# Revit family: 879-109X9X-002-DN50-600
name_source: partatom
category: Pipe Accessories
units: mm (PartAtom-declared; Revit-internal decimal feet)

## family parameters
Always vertical = Yes
Cut with Voids When Loaded = No
Part Type = Valve - Breaks Into
Round Connector Dimension = Use Diameter
Shared = No
Work Plane-Based = No

## types (42) — shared parameters
879-0050-10-144009A9C99 = DN50_PN10/16
879-0050-10-144009D9C99 = DN50_PN10/16
879-0065-10-144009A9C99 = DN65_PN10/16
879-0065-10-144009D9C99 = DN65_PN10/16
879-0080-10-144009A9C99 = DN80_PN10/16
879-0080-10-144009D9C99 = DN80_PN10/16
879-0100-10-144009A9C99 = DN100_PN10/16
879-0100-10-144009D9C99 = DN100_PN10/16
879-0150-10-144009A9C99 = DN150_PN10/16
879-0150-10-144009D9C99 = DN150_PN10/16
879-0200-10-044009A9C99 = DN200_PN10
879-0200-10-044009D9C99 = DN200_PN10
879-0200-10-144009A9C99 = DN200_PN16
879-0200-10-144009D9C99 = DN200_PN16
879-0250-10-044009A9C99 = DN250_PN10
879-0250-10-044009D9C99 = DN250_PN10
879-0250-10-144009A9C99 = DN250_PN16
879-0250-10-144009D9C99 = DN250_PN16
879-0300-10-044009A9C99 = DN300_PN10
879-0300-10-044009D9C99 = DN300_PN10
879-0300-10-144009A9C99 = DN300_PN16
879-0300-10-144009D9C99 = DN300_PN16
879-0350-10-044009A9C99 = DN350_PN10
879-0350-10-044009D9C99 = DN350_PN10
879-0350-10-144009A9C99 = DN350_PN16
879-0350-10-144009D9C99 = DN350_PN16
879-0400-10-044009A9C99 = DN400_PN10
879-0400-10-044009D9C99 = DN400_PN10
879-0400-10-144009A9C99 = DN400_PN16
879-0400-10-144009D9C99 = DN400_PN16
879-0450-10-044009A9C99 = DN450_PN10
879-0450-10-044009D9C99 = DN450_PN10
879-0450-10-144009A9C99 = DN450_PN16
879-0450-10-144009D9C99 = DN450_PN16
879-0500-10-044009A9C99 = DN500_PN10
879-0500-10-044009D9C99 = DN500_PN10
879-0500-10-144009A9C99 = DN500_PN16
879-0500-10-144009D9C99 = DN500_PN16
879-0600-10-044009A9C99 = DN600_PN10
879-0600-10-044009D9C99 = DN600_PN10
879-0600-10-144009A9C99 = DN600_PN16
879-0600-10-144009D9C99 = DN600_PN16
Body_wall_thickness = 10 mm  [stored 0.0328084 ft]
Description_ = AVK SINGLE SOLENOID CONTROL VALVE
Search_Table = 879-109X9X-002-DN50-600
URL product pages = https://www.avkvalves.com

## per-type parameters (varying)
- 879-0050-10-144009A9C99_DN50_PN10/16: Body_Collar_Dia=24 mm  [stored 0.0787402 ft]; Body_Collar_Dia_2=15 mm  [stored 0.0492126 ft]; Body_Flange_Dia=64 mm; Body_Flange_Dia_2=70 mm; Body_Height_1=58 mm; Body_Height_2=29 mm; Body_Height_3=45 mm; Body_Height_4=44 mm; Body_Top_Dia=9 mm  [stored 0.0295276 ft]; Body_Top_Dia_2=8 mm  [stored 0.0262467 ft]; Body_With_Dia=58 mm; Body_With_Dia_2=58 mm; Bolt_support=153 mm; Bolt_support_2=77 mm; Bolt_support_Dia=15 mm  [stored 0.0492126 ft]; Bolt_support_lenght=45 mm; Bolt_support_lenght_2=55 mm; Bottom_profile=13 mm; D1=50 mm; D3=83 mm; DN=50 mm; Fillet_Length=6 mm  [stored 0.019685 ft]; Flange_thickness=19 mm  [stored 0.062336 ft]; H3=341 mm; H3_ref=338 mm; ID=25 mm  [stored 0.082021 ft]; ID_2=19 mm  [stored 0.062336 ft]; L=230 mm; L_ref=96 mm; PG_Dia=25 mm  [stored 0.082021 ft]; PG_Ref=38 mm; PG_depth=8 mm  [stored 0.0262467 ft]; PG_ref=35 mm  [stored 0.114829 ft]; Pilot_Dia_1=15 mm  [stored 0.0492126 ft]; Pilot_Dia_2=30 mm  [stored 0.0984252 ft]; Pilot_Dia_3=10 mm  [stored 0.0328084 ft]; Pilot_Dia_4=5 mm  [stored 0.0164042 ft]; Pilot_Dia_5=3 mm  [stored 0.00984252 ft]; Pilot_top_1=211 mm; Pilot_top_ref=45 mm; Profile1_Height=135 mm; Profile1_Length=7 mm  [stored 0.0229659 ft]; Profile1_Length_2=5 mm  [stored 0.0164042 ft]; Profile_Dia=6 mm  [stored 0.019685 ft]; Profile_Dia_2=6 mm  [stored 0.019685 ft]; Profile_Dia_3=12 mm  [stored 0.0393701 ft]; Top_Profile=92 mm; Top_Profile_Ref=97 mm; Top_Profile_Ref_2=60 mm; Top_Profile_Ref_3=225 mm; W=259 mm; W_Ref=255 mm
- 879-0050-10-144009D9C99_DN50_PN10/16: Body_Collar_Dia=24 mm  [stored 0.0787402 ft]; Body_Collar_Dia_2=15 mm  [stored 0.0492126 ft]; Body_Flange_Dia=64 mm; Body_Flange_Dia_2=70 mm; Body_Height_1=58 mm; Body_Height_2=29 mm; Body_Height_3=50 mm; Body_Height_4=44 mm; Body_Top_Dia=9 mm  [stored 0.0295276 ft]; Body_Top_Dia_2=8 mm  [stored 0.0262467 ft]; Body_With_Dia=58 mm; Body_With_Dia_2=58 mm; Bolt_support=153 mm; Bolt_support_2=77 mm; Bolt_support_Dia=15 mm  [stored 0.0492126 ft]; Bolt_support_lenght=45 mm; Bolt_support_lenght_2=55 mm; Bottom_profile=13 mm; D1=50 mm; D3=83 mm; DN=50 mm; Fillet_Length=6 mm  [stored 0.019685 ft]; Flange_thickness=19 mm  [stored 0.062336 ft]; H3=341 mm; H3_ref=338 mm; ID=25 mm  [stored 0.082021 ft]; ID_2=19 mm  [stored 0.062336 ft]; L=230 mm; L_ref=96 mm; PG_Dia=25 mm  [stored 0.082021 ft]; PG_Ref=38 mm; PG_depth=8 mm  [stored 0.0262467 ft]; PG_ref=35 mm  [stored 0.114829 ft]; Pilot_Dia_1=15 mm  [stored 0.0492126 ft]; Pilot_Dia_2=30 mm  [stored 0.0984252 ft]; Pilot_Dia_3=10 mm  [stored 0.0328084 ft]; Pilot_Dia_4=5 mm  [stored 0.0164042 ft]; Pilot_Dia_5=3 mm  [stored 0.00984252 ft]; Pilot_top_1=213 mm; Pilot_top_ref=42 mm  [stored 0.137795 ft]; Profile1_Height=145 mm; Profile1_Length=7 mm  [stored 0.0229659 ft]; Profile1_Length_2=5 mm  [stored 0.0164042 ft]; Profile_Dia=6 mm  [stored 0.019685 ft]; Profile_Dia_2=6 mm  [stored 0.019685 ft]; Profile_Dia_3=12 mm  [stored 0.0393701 ft]; Top_Profile=92 mm; Top_Profile_Ref=97 mm; Top_Profile_Ref_2=55 mm; Top_Profile_Ref_3=228 mm; W=259 mm; W_Ref=255 mm
- 879-0065-10-144009A9C99_DN65_PN10/16: Body_Collar_Dia=30 mm  [stored 0.0984252 ft]; Body_Collar_Dia_2=19 mm  [stored 0.062336 ft]; Body_Flange_Dia=81 mm; Body_Flange_Dia_2=88 mm; Body_Height_1=73 mm; Body_Height_2=36 mm; Body_Height_3=58 mm; Body_Height_4=51 mm; Body_Top_Dia=12 mm  [stored 0.0393701 ft]; Body_Top_Dia_2=10 mm  [stored 0.0328084 ft]; Body_With_Dia=73 mm; Body_With_Dia_2=73 mm; Bolt_support=193 mm; Bolt_support_2=97 mm; Bolt_support_Dia=15 mm  [stored 0.0492126 ft]; Bolt_support_lenght=53 mm; Bolt_support_lenght_2=63 mm; Bottom_profile=16 mm  [stored 0.0524934 ft]; D1=59 mm; D3=93 mm; DN=65 mm; Fillet_Length=6 mm  [stored 0.019685 ft]; Flange_thickness=19 mm  [stored 0.062336 ft]; H3=372 mm; H3_ref=369 mm; ID=33 mm; ID_2=25 mm  [stored 0.082021 ft]; L=290 mm; L_ref=121 mm; PG_Dia=33 mm; PG_Ref=48 mm; PG_depth=8 mm  [stored 0.0262467 ft]; PG_ref=43 mm; Pilot_Dia_1=18 mm; Pilot_Dia_2=35 mm  [stored 0.114829 ft]; Pilot_Dia_3=12 mm  [stored 0.0393701 ft]; Pilot_Dia_4=6 mm  [stored 0.019685 ft]; Pilot_Dia_5=4 mm  [stored 0.0131234 ft]; Pilot_top_1=239 mm; Pilot_top_ref=37 mm; Profile1_Height=152 mm; Profile1_Length=8 mm  [stored 0.0262467 ft]; Profile1_Length_2=5 mm  [stored 0.0164042 ft]; Profile_Dia=6 mm  [stored 0.019685 ft]; Profile_Dia_2=6 mm  [stored 0.019685 ft]; Profile_Dia_3=12 mm  [stored 0.0393701 ft]; Top_Profile=116 mm; Top_Profile_Ref=121 mm; Top_Profile_Ref_2=62 mm; Top_Profile_Ref_3=245 mm; W=275 mm; W_Ref=271 mm
- 879-0065-10-144009D9C99_DN65_PN10/16: Body_Collar_Dia=30 mm  [stored 0.0984252 ft]; Body_Collar_Dia_2=19 mm  [stored 0.062336 ft]; Body_Flange_Dia=81 mm; Body_Flange_Dia_2=88 mm; Body_Height_1=73 mm; Body_Height_2=36 mm; Body_Height_3=73 mm; Body_Height_4=51 mm; Body_Top_Dia=12 mm  [stored 0.0393701 ft]; Body_Top_Dia_2=10 mm  [stored 0.0328084 ft]; Body_With_Dia=73 mm; Body_With_Dia_2=73 mm; Bolt_support=193 mm; Bolt_support_2=97 mm; Bolt_support_Dia=15 mm  [stored 0.0492126 ft]; Bolt_support_lenght=53 mm; Bolt_support_lenght_2=63 mm; Bottom_profile=16 mm  [stored 0.0524934 ft]; D1=59 mm; D3=93 mm; DN=65 mm; Fillet_Length=6 mm  [stored 0.019685 ft]; Flange_thickness=19 mm  [stored 0.062336 ft]; H3=372 mm; H3_ref=369 mm; ID=33 mm; ID_2=25 mm  [stored 0.082021 ft]; L=290 mm; L_ref=121 mm; PG_Dia=33 mm; PG_Ref=48 mm; PG_depth=8 mm  [stored 0.0262467 ft]; PG_ref=43 mm; Pilot_Dia_1=18 mm; Pilot_Dia_2=35 mm  [stored 0.114829 ft]; Pilot_Dia_3=12 mm  [stored 0.0393701 ft]; Pilot_Dia_4=6 mm  [stored 0.019685 ft]; Pilot_Dia_5=4 mm  [stored 0.0131234 ft]; Pilot_top_1=246 mm; Pilot_top_ref=30 mm  [stored 0.0984252 ft]; Profile1_Height=170 mm; Profile1_Length=8 mm  [stored 0.0262467 ft]; Profile1_Length_2=5 mm  [stored 0.0164042 ft]; Profile_Dia=6 mm  [stored 0.019685 ft]; Profile_Dia_2=6 mm  [stored 0.019685 ft]; Profile_Dia_3=12 mm  [stored 0.0393701 ft]; Top_Profile=116 mm; Top_Profile_Ref=121 mm; Top_Profile_Ref_2=53 mm; Top_Profile_Ref_3=250 mm; W=275 mm; W_Ref=271 mm
- 879-0080-10-144009A9C99_DN80_PN10/16: Body_Collar_Dia=32 mm  [stored 0.104987 ft]; Body_Collar_Dia_2=21 mm  [stored 0.0688976 ft]; Body_Flange_Dia=86 mm; Body_Flange_Dia_2=94 mm; Body_Height_1=78 mm; Body_Height_2=39 mm  [stored 0.127953 ft]; Body_Height_3=62 mm; Body_Height_4=54 mm; Body_Top_Dia=12 mm  [stored 0.0393701 ft]; Body_Top_Dia_2=10 mm  [stored 0.0328084 ft]; Body_With_Dia=78 mm; Body_With_Dia_2=78 mm; Bolt_support=207 mm; Bolt_support_2=103 mm; Bolt_support_Dia=15 mm  [stored 0.0492126 ft]; Bolt_support_lenght=60 mm; Bolt_support_lenght_2=70 mm; Bottom_profile=20 mm  [stored 0.0656168 ft]; D1=66 mm; D3=100 mm; DN=80 mm; Fillet_Length=6 mm  [stored 0.019685 ft]; Flange_thickness=19 mm  [stored 0.062336 ft]; H3=387 mm; H3_ref=384 mm; ID=40 mm  [stored 0.131234 ft]; ID_2=31 mm  [stored 0.101706 ft]; L=310 mm; L_ref=129 mm; PG_Dia=40 mm  [stored 0.131234 ft]; PG_Ref=52 mm; PG_depth=8 mm  [stored 0.0262467 ft]; PG_ref=50 mm; Pilot_Dia_1=20 mm  [stored 0.0656168 ft]; Pilot_Dia_2=39 mm  [stored 0.127953 ft]; Pilot_Dia_3=13 mm; Pilot_Dia_4=7 mm  [stored 0.0229659 ft]; Pilot_Dia_5=4 mm  [stored 0.0131234 ft]; Pilot_top_1=249 mm; Pilot_top_ref=35 mm  [stored 0.114829 ft]; Profile1_Height=179 mm; Profile1_Length=8 mm  [stored 0.0262467 ft]; Profile1_Length_2=6 mm  [stored 0.019685 ft]; Profile_Dia=6 mm  [stored 0.019685 ft]; Profile_Dia_2=6 mm  [stored 0.019685 ft]; Profile_Dia_3=12 mm  [stored 0.0393701 ft]; Top_Profile=124 mm; Top_Profile_Ref=129 mm; Top_Profile_Ref_2=53 mm; Top_Profile_Ref_3=258 mm; W=290 mm; W_Ref=286 mm
- 879-0080-10-144009D9C99_DN80_PN10/16: Body_Collar_Dia=32 mm  [stored 0.104987 ft]; Body_Collar_Dia_2=21 mm  [stored 0.0688976 ft]; Body_Flange_Dia=86 mm; Body_Flange_Dia_2=94 mm; Body_Height_1=78 mm; Body_Height_2=39 mm  [stored 0.127953 ft]; Body_Height_3=78 mm; Body_Height_4=54 mm; Body_Top_Dia=12 mm  [stored 0.0393701 ft]; Body_Top_Dia_2=10 mm  [stored 0.0328084 ft]; Body_With_Dia=78 mm; Body_With_Dia_2=78 mm; Bolt_support=207 mm; Bolt_support_2=103 mm; Bolt_support_Dia=15 mm  [stored 0.0492126 ft]; Bolt_support_lenght=60 mm; Bolt_support_lenght_2=70 mm; Bottom_profile=20 mm  [stored 0.0656168 ft]; D1=66 mm; D3=100 mm; DN=80 mm; Fillet_Length=6 mm  [stored 0.019685 ft]; Flange_thickness=19 mm  [stored 0.062336 ft]; H3=387 mm; H3_ref=384 mm; ID=40 mm  [stored 0.131234 ft]; ID_2=31 mm  [stored 0.101706 ft]; L=310 mm; L_ref=129 mm; PG_Dia=40 mm  [stored 0.131234 ft]; PG_Ref=52 mm; PG_depth=8 mm  [stored 0.0262467 ft]; PG_ref=50 mm; Pilot_Dia_1=20 mm  [stored 0.0656168 ft]; Pilot_Dia_2=39 mm  [stored 0.127953 ft]; Pilot_Dia_3=13 mm; Pilot_Dia_4=7 mm  [stored 0.0229659 ft]; Pilot_Dia_5=4 mm  [stored 0.0131234 ft]; Pilot_top_1=256 mm; Pilot_top_ref=28 mm  [stored 0.0918635 ft]; Profile1_Height=168 mm; Profile1_Length=8 mm  [stored 0.0262467 ft]; Profile1_Length_2=6 mm  [stored 0.019685 ft]; Profile_Dia=6 mm  [stored 0.019685 ft]; Profile_Dia_2=6 mm  [stored 0.019685 ft]; Profile_Dia_3=12 mm  [stored 0.0393701 ft]; Top_Profile=124 mm; Top_Profile_Ref=129 mm; Top_Profile_Ref_2=58 mm; Top_Profile_Ref_3=255 mm; W=290 mm; W_Ref=286 mm
- 879-0100-10-144009A9C99_DN100_PN10/16: Body_Collar_Dia=36 mm; Body_Collar_Dia_2=23 mm  [stored 0.0754593 ft]; Body_Flange_Dia=97 mm; Body_Flange_Dia_2=106 mm; Body_Height_1=88 mm; Body_Height_2=44 mm; Body_Height_3=59 mm; Body_Height_4=59 mm; Body_Top_Dia=14 mm  [stored 0.0459318 ft]; Body_Top_Dia_2=12 mm  [stored 0.0393701 ft]; Body_With_Dia=88 mm; Body_With_Dia_2=88 mm; Bolt_support=233 mm; Bolt_support_2=117 mm; Bolt_support_Dia=15 mm  [stored 0.0492126 ft]; Bolt_support_lenght=70 mm; Bolt_support_lenght_2=80 mm; Bottom_profile=25 mm  [stored 0.082021 ft]; D1=78 mm; D3=110 mm; DN=100 mm; Fillet_Length=6 mm  [stored 0.019685 ft]; Flange_thickness=19 mm  [stored 0.062336 ft]; H3=410 mm; H3_ref=407 mm; ID=50 mm; ID_2=38 mm; L=350 mm; L_ref=146 mm; PG_Dia=50 mm; PG_Ref=58 mm; PG_depth=8 mm  [stored 0.0262467 ft]; PG_ref=60 mm; Pilot_Dia_1=22 mm  [stored 0.0721785 ft]; Pilot_Dia_2=44 mm; Pilot_Dia_3=15 mm  [stored 0.0492126 ft]; Pilot_Dia_4=7 mm  [stored 0.0229659 ft]; Pilot_Dia_5=5 mm  [stored 0.0164042 ft]; Pilot_top_1=261 mm; Pilot_top_ref=36 mm; Profile1_Height=185 mm; Profile1_Length=9 mm  [stored 0.0295276 ft]; Profile1_Length_2=6 mm  [stored 0.019685 ft]; Profile_Dia=6 mm  [stored 0.019685 ft]; Profile_Dia_2=6 mm  [stored 0.019685 ft]; Profile_Dia_3=12 mm  [stored 0.0393701 ft]; Top_Profile=140 mm; Top_Profile_Ref=145 mm; Top_Profile_Ref_2=56 mm; Top_Profile_Ref_3=269 mm; W=310 mm; W_Ref=306 mm
- 879-0100-10-144009D9C99_DN100_PN10/16: Body_Collar_Dia=36 mm; Body_Collar_Dia_2=23 mm  [stored 0.0754593 ft]; Body_Flange_Dia=97 mm; Body_Flange_Dia_2=106 mm; Body_Height_1=88 mm; Body_Height_2=44 mm; Body_Height_3=70 mm; Body_Height_4=59 mm; Body_Top_Dia=14 mm  [stored 0.0459318 ft]; Body_Top_Dia_2=12 mm  [stored 0.0393701 ft]; Body_With_Dia=88 mm; Body_With_Dia_2=88 mm; Bolt_support=233 mm; Bolt_support_2=117 mm; Bolt_support_Dia=15 mm  [stored 0.0492126 ft]; Bolt_support_lenght=70 mm; Bolt_support_lenght_2=80 mm; Bottom_profile=25 mm  [stored 0.082021 ft]; D1=78 mm; D3=110 mm; DN=100 mm; Fillet_Length=6 mm  [stored 0.019685 ft]; Flange_thickness=19 mm  [stored 0.062336 ft]; H3=410 mm; H3_ref=407 mm; ID=50 mm; ID_2=39 mm  [stored 0.127953 ft]; L=350 mm; L_ref=146 mm; PG_Dia=50 mm; PG_Ref=58 mm; PG_depth=8 mm  [stored 0.0262467 ft]; PG_ref=60 mm; Pilot_Dia_1=22 mm  [stored 0.0721785 ft]; Pilot_Dia_2=44 mm; Pilot_Dia_3=15 mm  [stored 0.0492126 ft]; Pilot_Dia_4=7 mm  [stored 0.0229659 ft]; Pilot_Dia_5=5 mm  [stored 0.0164042 ft]; Pilot_top_1=267 mm; Pilot_top_ref=30 mm  [stored 0.0984252 ft]; Profile1_Height=176 mm; Profile1_Length=9 mm  [stored 0.0295276 ft]; Profile1_Length_2=6 mm  [stored 0.019685 ft]; Profile_Dia=6 mm  [stored 0.019685 ft]; Profile_Dia_2=6 mm  [stored 0.019685 ft]; Profile_Dia_3=12 mm  [stored 0.0393701 ft]; Top_Profile=140 mm; Top_Profile_Ref=145 mm; Top_Profile_Ref_2=61 mm; Top_Profile_Ref_3=267 mm; W=310 mm; W_Ref=306 mm
- 879-0150-10-144009A9C99_DN150_PN10/16: Body_Collar_Dia=50 mm; Body_Collar_Dia_2=32 mm  [stored 0.104987 ft]; Body_Flange_Dia=133 mm; Body_Flange_Dia_2=145 mm; Body_Height_1=120 mm; Body_Height_2=60 mm; Body_Height_3=60 mm; Body_Height_4=75 mm; Body_Top_Dia=19 mm  [stored 0.062336 ft]; Body_Top_Dia_2=16 mm  [stored 0.0524934 ft]; Body_With_Dia=120 mm; Body_With_Dia_2=120 mm; Bolt_support=320 mm; Bolt_support_2=160 mm; Bolt_support_Dia=20 mm  [stored 0.0656168 ft]; Bolt_support_lenght=95 mm; Bolt_support_lenght_2=105 mm; Bottom_profile=38 mm; D1=106 mm; D3=143 mm; DN=150 mm; Fillet_Length=8 mm  [stored 0.0262467 ft]; Flange_thickness=19 mm  [stored 0.062336 ft]; H3=543 mm; H3_ref=539 mm; ID=75 mm; ID_2=58 mm; L=480 mm; L_ref=200 mm; PG_Dia=50 mm; PG_Ref=80 mm; PG_depth=11 mm; PG_ref=85 mm; Pilot_Dia_1=31 mm  [stored 0.101706 ft]; Pilot_Dia_2=62 mm; Pilot_Dia_3=21 mm  [stored 0.0688976 ft]; Pilot_Dia_4=10 mm  [stored 0.0328084 ft]; Pilot_Dia_5=7 mm  [stored 0.0229659 ft]; Pilot_top_1=336 mm; Pilot_top_ref=61 mm; Profile1_Height=230 mm; Profile1_Length=12 mm  [stored 0.0393701 ft]; Profile1_Length_2=8 mm  [stored 0.0262467 ft]; Profile_Dia=8 mm  [stored 0.0262467 ft]; Profile_Dia_2=8 mm  [stored 0.0262467 ft]; Profile_Dia_3=16 mm  [stored 0.0524934 ft]; Top_Profile=192 mm; Top_Profile_Ref=197 mm; Top_Profile_Ref_2=83 mm; Top_Profile_Ref_3=355 mm; W=375 mm; W_Ref=369 mm
- 879-0150-10-144009D9C99_DN150_PN10/16: Body_Collar_Dia=50 mm; Body_Collar_Dia_2=32 mm  [stored 0.104987 ft]; Body_Flange_Dia=133 mm; Body_Flange_Dia_2=145 mm; Body_Height_1=120 mm; Body_Height_2=60 mm; Body_Height_3=68 mm; Body_Height_4=75 mm; Body_Top_Dia=19 mm  [stored 0.062336 ft]; Body_Top_Dia_2=16 mm  [stored 0.0524934 ft]; Body_With_Dia=120 mm; Body_With_Dia_2=120 mm; Bolt_support=320 mm; Bolt_support_2=160 mm; Bolt_support_Dia=20 mm  [stored 0.0656168 ft]; Bolt_support_lenght=95 mm; Bolt_support_lenght_2=105 mm; Bottom_profile=38 mm; D1=106 mm; D3=143 mm; DN=150 mm; Fillet_Length=8 mm  [stored 0.0262467 ft]; Flange_thickness=19 mm  [stored 0.062336 ft]; H3=543 mm; H3_ref=539 mm; ID=75 mm; ID_2=58 mm; L=480 mm; L_ref=200 mm; PG_Dia=50 mm; PG_Ref=80 mm; PG_depth=11 mm; PG_ref=85 mm; Pilot_Dia_1=31 mm  [stored 0.101706 ft]; Pilot_Dia_2=62 mm; Pilot_Dia_3=21 mm  [stored 0.0688976 ft]; Pilot_Dia_4=10 mm  [stored 0.0328084 ft]; Pilot_Dia_5=7 mm  [stored 0.0229659 ft]; Pilot_top_1=340 mm; Pilot_top_ref=57 mm; Profile1_Height=230 mm; Profile1_Length=12 mm  [stored 0.0393701 ft]; Profile1_Length_2=8 mm  [stored 0.0262467 ft]; Profile_Dia=8 mm  [stored 0.0262467 ft]; Profile_Dia_2=8 mm  [stored 0.0262467 ft]; Profile_Dia_3=16 mm  [stored 0.0524934 ft]; Top_Profile=192 mm; Top_Profile_Ref=197 mm; Top_Profile_Ref_2=83 mm; Top_Profile_Ref_3=355 mm; W=375 mm; W_Ref=369 mm
- 879-0200-10-044009A9C99_DN200_PN10: Body_Collar_Dia=63 mm; Body_Collar_Dia_2=40 mm  [stored 0.131234 ft]; Body_Flange_Dia=167 mm; Body_Flange_Dia_2=182 mm; Body_Height_1=150 mm; Body_Height_2=75 mm; Body_Height_3=75 mm; Body_Height_4=90 mm; Body_Top_Dia=24 mm  [stored 0.0787402 ft]; Body_Top_Dia_2=20 mm  [stored 0.0656168 ft]; Body_With_Dia=150 mm; Body_With_Dia_2=150 mm; Bolt_support=400 mm; Bolt_support_2=200 mm; Bolt_support_Dia=25 mm  [stored 0.082021 ft]; Bolt_support_lenght=120 mm; Bolt_support_lenght_2=130 mm; Bottom_profile=50 mm; D1=133 mm; D3=170 mm; DN=200 mm; Fillet_Length=10 mm  [stored 0.0328084 ft]; Flange_thickness=20 mm  [stored 0.0656168 ft]; H3=657 mm; H3_ref=652 mm; ID=100 mm; ID_2=77 mm; L=600 mm; L_ref=250 mm; PG_Dia=67 mm; PG_Ref=100 mm; PG_depth=14 mm  [stored 0.0459318 ft]; PG_ref=110 mm; Pilot_Dia_1=39 mm  [stored 0.127953 ft]; Pilot_Dia_2=77 mm; Pilot_Dia_3=26 mm; Pilot_Dia_4=13 mm; Pilot_Dia_5=9 mm  [stored 0.0295276 ft]; Pilot_top_1=409 mm; Pilot_top_ref=74 mm; Profile1_Height=273 mm; Profile1_Length=14 mm  [stored 0.0459318 ft]; Profile1_Length_2=9 mm  [stored 0.0295276 ft]; Profile_Dia=10 mm  [stored 0.0328084 ft]; Profile_Dia_2=10 mm  [stored 0.0328084 ft]; Profile_Dia_3=20 mm  [stored 0.0656168 ft]; Top_Profile=240 mm; Top_Profile_Ref=245 mm; Top_Profile_Ref_2=105 mm; Top_Profile_Ref_3=430 mm; W=445 mm; W_Ref=438 mm
- 879-0200-10-044009D9C99_DN200_PN10: Body_Collar_Dia=63 mm; Body_Collar_Dia_2=40 mm  [stored 0.131234 ft]; Body_Flange_Dia=167 mm; Body_Flange_Dia_2=182 mm; Body_Height_1=150 mm; Body_Height_2=75 mm; Body_Height_3=100 mm; Body_Height_4=90 mm; Body_Top_Dia=24 mm  [stored 0.0787402 ft]; Body_Top_Dia_2=20 mm  [stored 0.0656168 ft]; Body_With_Dia=150 mm; Body_With_Dia_2=150 mm; Bolt_support=400 mm; Bolt_support_2=200 mm; Bolt_support_Dia=25 mm  [stored 0.082021 ft]; Bolt_support_lenght=120 mm; Bolt_support_lenght_2=130 mm; Bottom_profile=50 mm; D1=133 mm; D3=170 mm; DN=200 mm; Fillet_Length=10 mm  [stored 0.0328084 ft]; Flange_thickness=20 mm  [stored 0.0656168 ft]; H3=657 mm; H3_ref=652 mm; ID=100 mm; ID_2=77 mm; L=600 mm; L_ref=250 mm; PG_Dia=67 mm; PG_Ref=100 mm; PG_depth=14 mm  [stored 0.0459318 ft]; PG_ref=110 mm; Pilot_Dia_1=39 mm  [stored 0.127953 ft]; Pilot_Dia_2=77 mm; Pilot_Dia_3=26 mm; Pilot_Dia_4=13 mm; Pilot_Dia_5=9 mm  [stored 0.0295276 ft]; Pilot_top_1=421 mm; Pilot_top_ref=61 mm; Profile1_Height=275 mm; Profile1_Length=14 mm  [stored 0.0459318 ft]; Profile1_Length_2=9 mm  [stored 0.0295276 ft]; Profile_Dia=10 mm  [stored 0.0328084 ft]; Profile_Dia_2=10 mm  [stored 0.0328084 ft]; Profile_Dia_3=20 mm  [stored 0.0656168 ft]; Top_Profile=240 mm; Top_Profile_Ref=245 mm; Top_Profile_Ref_2=104 mm; Top_Profile_Ref_3=430 mm; W=445 mm; W_Ref=438 mm
- 879-0200-10-144009A9C99_DN200_PN16: Body_Collar_Dia=63 mm; Body_Collar_Dia_2=40 mm  [stored 0.131234 ft]; Body_Flange_Dia=167 mm; Body_Flange_Dia_2=182 mm; Body_Height_1=150 mm; Body_Height_2=75 mm; Body_Height_3=75 mm; Body_Height_4=90 mm; Body_Top_Dia=24 mm  [stored 0.0787402 ft]; Body_Top_Dia_2=20 mm  [stored 0.0656168 ft]; Body_With_Dia=150 mm; Body_With_Dia_2=150 mm; Bolt_support=400 mm; Bolt_support_2=200 mm; Bolt_support_Dia=25 mm  [stored 0.082021 ft]; Bolt_support_lenght=120 mm; Bolt_support_lenght_2=130 mm; Bottom_profile=50 mm; D1=133 mm; D3=170 mm; DN=200 mm; Fillet_Length=10 mm  [stored 0.0328084 ft]; Flange_thickness=20 mm  [stored 0.0656168 ft]; H3=657 mm; H3_ref=652 mm; ID=100 mm; ID_2=77 mm; L=600 mm; L_ref=250 mm; PG_Dia=67 mm; PG_Ref=100 mm; PG_depth=14 mm  [stored 0.0459318 ft]; PG_ref=110 mm; Pilot_Dia_1=39 mm  [stored 0.127953 ft]; Pilot_Dia_2=77 mm; Pilot_Dia_3=26 mm; Pilot_Dia_4=13 mm; Pilot_Dia_5=9 mm  [stored 0.0295276 ft]; Pilot_top_1=409 mm; Pilot_top_ref=74 mm; Profile1_Height=273 mm; Profile1_Length=14 mm  [stored 0.0459318 ft]; Profile1_Length_2=9 mm  [stored 0.0295276 ft]; Profile_Dia=10 mm  [stored 0.0328084 ft]; Profile_Dia_2=10 mm  [stored 0.0328084 ft]; Profile_Dia_3=20 mm  [stored 0.0656168 ft]; Top_Profile=240 mm; Top_Profile_Ref=245 mm; Top_Profile_Ref_2=105 mm; Top_Profile_Ref_3=430 mm; W=445 mm; W_Ref=438 mm
- 879-0200-10-144009D9C99_DN200_PN16: Body_Collar_Dia=63 mm; Body_Collar_Dia_2=40 mm  [stored 0.131234 ft]; Body_Flange_Dia=167 mm; Body_Flange_Dia_2=182 mm; Body_Height_1=150 mm; Body_Height_2=75 mm; Body_Height_3=86 mm; Body_Height_4=90 mm; Body_Top_Dia=24 mm  [stored 0.0787402 ft]; Body_Top_Dia_2=20 mm  [stored 0.0656168 ft]; Body_With_Dia=150 mm; Body_With_Dia_2=150 mm; Bolt_support=400 mm; Bolt_support_2=200 mm; Bolt_support_Dia=25 mm  [stored 0.082021 ft]; Bolt_support_lenght=120 mm; Bolt_support_lenght_2=130 mm; Bottom_profile=50 mm; D1=133 mm; D3=170 mm; DN=200 mm; Fillet_Length=10 mm  [stored 0.0328084 ft]; Flange_thickness=20 mm  [stored 0.0656168 ft]; H3=657 mm; H3_ref=652 mm; ID=100 mm; ID_2=77 mm; L=600 mm; L_ref=250 mm; PG_Dia=67 mm; PG_Ref=100 mm; PG_depth=14 mm  [stored 0.0459318 ft]; PG_ref=110 mm; Pilot_Dia_1=39 mm  [stored 0.127953 ft]; Pilot_Dia_2=77 mm; Pilot_Dia_3=26 mm; Pilot_Dia_4=13 mm; Pilot_Dia_5=9 mm  [stored 0.0295276 ft]; Pilot_top_1=414 mm; Pilot_top_ref=68 mm; Profile1_Height=275 mm; Profile1_Length=14 mm  [stored 0.0459318 ft]; Profile1_Length_2=9 mm  [stored 0.0295276 ft]; Profile_Dia=10 mm  [stored 0.0328084 ft]; Profile_Dia_2=10 mm  [stored 0.0328084 ft]; Profile_Dia_3=20 mm  [stored 0.0656168 ft]; Top_Profile=240 mm; Top_Profile_Ref=245 mm; Top_Profile_Ref_2=104 mm; Top_Profile_Ref_3=430 mm; W=445 mm; W_Ref=438 mm
- 879-0250-10-044009A9C99_DN250_PN10: Body_Collar_Dia=76 mm; Body_Collar_Dia_2=49 mm; Body_Flange_Dia=203 mm; Body_Flange_Dia_2=221 mm; Body_Height_1=183 mm; Body_Height_2=91 mm; Body_Height_3=81 mm; Body_Height_4=106 mm; Body_Top_Dia=29 mm; Body_Top_Dia_2=24 mm  [stored 0.0787402 ft]; Body_With_Dia=183 mm; Body_With_Dia_2=183 mm; Bolt_support=487 mm; Bolt_support_2=243 mm; Bolt_support_Dia=25 mm  [stored 0.082021 ft]; Bolt_support_lenght=145 mm; Bolt_support_lenght_2=155 mm; Bottom_profile=63 mm; D1=160 mm; D3=198 mm; DN=250 mm; Fillet_Length=10 mm  [stored 0.0328084 ft]; Flange_thickness=22 mm  [stored 0.0721785 ft]; H3=692 mm; H3_ref=687 mm; ID=125 mm; ID_2=96 mm; L=730 mm; L_ref=304 mm; PG_Dia=83 mm; PG_Ref=122 mm; PG_depth=14 mm  [stored 0.0459318 ft]; PG_ref=135 mm; Pilot_Dia_1=46 mm; Pilot_Dia_2=92 mm; Pilot_Dia_3=31 mm  [stored 0.101706 ft]; Pilot_Dia_4=15 mm  [stored 0.0492126 ft]; Pilot_Dia_5=10 mm  [stored 0.0328084 ft]; Pilot_top_1=440 mm; Pilot_top_ref=50 mm; Profile1_Height=327 mm; Profile1_Length=16 mm  [stored 0.0524934 ft]; Profile1_Length_2=11 mm; Profile_Dia=10 mm  [stored 0.0328084 ft]; Profile_Dia_2=10 mm  [stored 0.0328084 ft]; Profile_Dia_3=20 mm  [stored 0.0656168 ft]; Top_Profile=292 mm; Top_Profile_Ref=297 mm; Top_Profile_Ref_2=81 mm; Top_Profile_Ref_3=449 mm; W=525 mm; W_Ref=518 mm
- 879-0250-10-044009D9C99_DN250_PN10: Body_Collar_Dia=76 mm; Body_Collar_Dia_2=49 mm; Body_Flange_Dia=203 mm; Body_Flange_Dia_2=221 mm; Body_Height_1=183 mm; Body_Height_2=91 mm; Body_Height_3=105 mm; Body_Height_4=106 mm; Body_Top_Dia=29 mm; Body_Top_Dia_2=24 mm  [stored 0.0787402 ft]; Body_With_Dia=183 mm; Body_With_Dia_2=183 mm; Bolt_support=487 mm; Bolt_support_2=243 mm; Bolt_support_Dia=25 mm  [stored 0.082021 ft]; Bolt_support_lenght=145 mm; Bolt_support_lenght_2=155 mm; Bottom_profile=63 mm; D1=160 mm; D3=198 mm; DN=250 mm; Fillet_Length=10 mm  [stored 0.0328084 ft]; Flange_thickness=22 mm  [stored 0.0721785 ft]; H3=692 mm; H3_ref=687 mm; ID=125 mm; ID_2=96 mm; L=730 mm; L_ref=304 mm; PG_Dia=83 mm; PG_Ref=122 mm; PG_depth=14 mm  [stored 0.0459318 ft]; PG_ref=135 mm; Pilot_Dia_1=46 mm; Pilot_Dia_2=92 mm; Pilot_Dia_3=31 mm  [stored 0.101706 ft]; Pilot_Dia_4=15 mm  [stored 0.0492126 ft]; Pilot_Dia_5=10 mm  [stored 0.0328084 ft]; Pilot_top_1=451 mm; Pilot_top_ref=38 mm; Profile1_Height=330 mm; Profile1_Length=16 mm  [stored 0.0524934 ft]; Profile1_Length_2=11 mm; Profile_Dia=10 mm  [stored 0.0328084 ft]; Profile_Dia_2=10 mm  [stored 0.0328084 ft]; Profile_Dia_3=20 mm  [stored 0.0656168 ft]; Top_Profile=292 mm; Top_Profile_Ref=297 mm; Top_Profile_Ref_2=80 mm; Top_Profile_Ref_3=450 mm; W=525 mm; W_Ref=518 mm
- 879-0250-10-144009A9C99_DN250_PN16: Body_Collar_Dia=76 mm; Body_Collar_Dia_2=49 mm; Body_Flange_Dia=203 mm; Body_Flange_Dia_2=221 mm; Body_Height_1=183 mm; Body_Height_2=91 mm; Body_Height_3=81 mm; Body_Height_4=106 mm; Body_Top_Dia=29 mm; Body_Top_Dia_2=24 mm  [stored 0.0787402 ft]; Body_With_Dia=183 mm; Body_With_Dia_2=183 mm; Bolt_support=487 mm; Bolt_support_2=243 mm; Bolt_support_Dia=25 mm  [stored 0.082021 ft]; Bolt_support_lenght=145 mm; Bolt_support_lenght_2=155 mm; Bottom_profile=63 mm; D1=160 mm; D3=203 mm; DN=250 mm; Fillet_Length=10 mm  [stored 0.0328084 ft]; Flange_thickness=22 mm  [stored 0.0721785 ft]; H3=692 mm; H3_ref=687 mm; ID=125 mm; ID_2=96 mm; L=730 mm; L_ref=304 mm; PG_Dia=83 mm; PG_Ref=122 mm; PG_depth=14 mm  [stored 0.0459318 ft]; PG_ref=135 mm; Pilot_Dia_1=47 mm; Pilot_Dia_2=94 mm; Pilot_Dia_3=31 mm  [stored 0.101706 ft]; Pilot_Dia_4=16 mm  [stored 0.0524934 ft]; Pilot_Dia_5=10 mm  [stored 0.0328084 ft]; Pilot_top_1=437 mm; Pilot_top_ref=47 mm; Profile1_Height=335 mm; Profile1_Length=17 mm; Profile1_Length_2=11 mm; Profile_Dia=10 mm  [stored 0.0328084 ft]; Profile_Dia_2=10 mm  [stored 0.0328084 ft]; Profile_Dia_3=20 mm  [stored 0.0656168 ft]; Top_Profile=292 mm; Top_Profile_Ref=297 mm; Top_Profile_Ref_2=75 mm; Top_Profile_Ref_3=447 mm; W=525 mm; W_Ref=518 mm
- 879-0250-10-144009D9C99_DN250_PN16: Body_Collar_Dia=76 mm; Body_Collar_Dia_2=49 mm; Body_Flange_Dia=203 mm; Body_Flange_Dia_2=221 mm; Body_Height_1=183 mm; Body_Height_2=91 mm; Body_Height_3=81 mm; Body_Height_4=106 mm; Body_Top_Dia=29 mm; Body_Top_Dia_2=24 mm  [stored 0.0787402 ft]; Body_With_Dia=183 mm; Body_With_Dia_2=183 mm; Bolt_support=487 mm; Bolt_support_2=243 mm; Bolt_support_Dia=25 mm  [stored 0.082021 ft]; Bolt_support_lenght=145 mm; Bolt_support_lenght_2=155 mm; Bottom_profile=63 mm; D1=160 mm; D3=203 mm; DN=250 mm; Fillet_Length=10 mm  [stored 0.0328084 ft]; Flange_thickness=22 mm  [stored 0.0721785 ft]; H3=692 mm; H3_ref=687 mm; ID=125 mm; ID_2=96 mm; L=730 mm; L_ref=304 mm; PG_Dia=83 mm; PG_Ref=122 mm; PG_depth=14 mm  [stored 0.0459318 ft]; PG_ref=135 mm; Pilot_Dia_1=47 mm; Pilot_Dia_2=94 mm; Pilot_Dia_3=31 mm  [stored 0.101706 ft]; Pilot_Dia_4=16 mm  [stored 0.0524934 ft]; Pilot_Dia_5=10 mm  [stored 0.0328084 ft]; Pilot_top_1=437 mm; Pilot_top_ref=47 mm; Profile1_Height=350 mm; Profile1_Length=17 mm; Profile1_Length_2=11 mm; Profile_Dia=10 mm  [stored 0.0328084 ft]; Profile_Dia_2=10 mm  [stored 0.0328084 ft]; Profile_Dia_3=20 mm  [stored 0.0656168 ft]; Top_Profile=292 mm; Top_Profile_Ref=297 mm; Top_Profile_Ref_2=67 mm; Top_Profile_Ref_3=451 mm; W=525 mm; W_Ref=518 mm
- 879-0300-10-044009A9C99_DN300_PN10: Body_Collar_Dia=89 mm; Body_Collar_Dia_2=57 mm; Body_Flange_Dia=236 mm; Body_Flange_Dia_2=258 mm; Body_Height_1=213 mm; Body_Height_2=106 mm; Body_Height_3=95 mm; Body_Height_4=121 mm; Body_Top_Dia=34 mm; Body_Top_Dia_2=28 mm  [stored 0.0918635 ft]; Body_With_Dia=213 mm; Body_With_Dia_2=213 mm; Bolt_support=567 mm; Bolt_support_2=283 mm; Bolt_support_Dia=25 mm  [stored 0.082021 ft]; Bolt_support_lenght=170 mm; Bolt_support_lenght_2=180 mm; Bottom_profile=75 mm; D1=185 mm; D3=223 mm; DN=300 mm; Fillet_Length=10 mm  [stored 0.0328084 ft]; Flange_thickness=25 mm  [stored 0.082021 ft]; H3=761 mm; H3_ref=756 mm; ID=150 mm; ID_2=115 mm; L=850 mm; L_ref=354 mm; PG_Dia=100 mm; PG_Ref=142 mm; PG_depth=14 mm  [stored 0.0459318 ft]; PG_ref=160 mm; Pilot_Dia_1=53 mm; Pilot_Dia_2=105 mm; Pilot_Dia_3=35 mm  [stored 0.114829 ft]; Pilot_Dia_4=18 mm; Pilot_Dia_5=12 mm  [stored 0.0393701 ft]; Pilot_top_1=491 mm; Pilot_top_ref=43 mm; Profile1_Height=361 mm; Profile1_Length=19 mm  [stored 0.062336 ft]; Profile1_Length_2=12 mm  [stored 0.0393701 ft]; Profile_Dia=10 mm  [stored 0.0328084 ft]; Profile_Dia_2=10 mm  [stored 0.0328084 ft]; Profile_Dia_3=20 mm  [stored 0.0656168 ft]; Top_Profile=340 mm; Top_Profile_Ref=345 mm; Top_Profile_Ref_2=86 mm; Top_Profile_Ref_3=490 mm; W=590 mm; W_Ref=583 mm
- 879-0300-10-044009D9C99_DN300_PN10: Body_Collar_Dia=89 mm; Body_Collar_Dia_2=57 mm; Body_Flange_Dia=236 mm; Body_Flange_Dia_2=258 mm; Body_Height_1=213 mm; Body_Height_2=106 mm; Body_Height_3=106 mm; Body_Height_4=121 mm; Body_Top_Dia=34 mm; Body_Top_Dia_2=28 mm  [stored 0.0918635 ft]; Body_With_Dia=213 mm; Body_With_Dia_2=213 mm; Bolt_support=567 mm; Bolt_support_2=283 mm; Bolt_support_Dia=25 mm  [stored 0.082021 ft]; Bolt_support_lenght=170 mm; Bolt_support_lenght_2=180 mm; Bottom_profile=75 mm; D1=185 mm; D3=223 mm; DN=300 mm; Fillet_Length=10 mm  [stored 0.0328084 ft]; Flange_thickness=25 mm  [stored 0.082021 ft]; H3=761 mm; H3_ref=756 mm; ID=150 mm; ID_2=115 mm; L=850 mm; L_ref=354 mm; PG_Dia=100 mm; PG_Ref=142 mm; PG_depth=14 mm  [stored 0.0459318 ft]; PG_ref=160 mm; Pilot_Dia_1=53 mm; Pilot_Dia_2=105 mm; Pilot_Dia_3=35 mm  [stored 0.114829 ft]; Pilot_Dia_4=18 mm; Pilot_Dia_5=12 mm  [stored 0.0393701 ft]; Pilot_top_1=497 mm; Pilot_top_ref=37 mm; Profile1_Height=400 mm; Profile1_Length=19 mm  [stored 0.062336 ft]; Profile1_Length_2=12 mm  [stored 0.0393701 ft]; Profile_Dia=10 mm  [stored 0.0328084 ft]; Profile_Dia_2=10 mm  [stored 0.0328084 ft]; Profile_Dia_3=20 mm  [stored 0.0656168 ft]; Top_Profile=340 mm; Top_Profile_Ref=345 mm; Top_Profile_Ref_2=67 mm; Top_Profile_Ref_3=500 mm; W=590 mm; W_Ref=583 mm
- 879-0300-10-144009A9C99_DN300_PN16: Body_Collar_Dia=89 mm; Body_Collar_Dia_2=57 mm; Body_Flange_Dia=236 mm; Body_Flange_Dia_2=258 mm; Body_Height_1=213 mm; Body_Height_2=106 mm; Body_Height_3=95 mm; Body_Height_4=121 mm; Body_Top_Dia=34 mm; Body_Top_Dia_2=28 mm  [stored 0.0918635 ft]; Body_With_Dia=213 mm; Body_With_Dia_2=213 mm; Bolt_support=567 mm; Bolt_support_2=283 mm; Bolt_support_Dia=25 mm  [stored 0.082021 ft]; Bolt_support_lenght=170 mm; Bolt_support_lenght_2=180 mm; Bottom_profile=75 mm; D1=185 mm; D3=230 mm; DN=300 mm; Fillet_Length=10 mm  [stored 0.0328084 ft]; Flange_thickness=25 mm  [stored 0.082021 ft]; H3=761 mm; H3_ref=756 mm; ID=150 mm; ID_2=115 mm; L=850 mm; L_ref=354 mm; PG_Dia=100 mm; PG_Ref=142 mm; PG_depth=14 mm  [stored 0.0459318 ft]; PG_ref=160 mm; Pilot_Dia_1=55 mm; Pilot_Dia_2=109 mm; Pilot_Dia_3=36 mm; Pilot_Dia_4=18 mm; Pilot_Dia_5=12 mm  [stored 0.0393701 ft]; Pilot_top_1=487 mm; Pilot_top_ref=39 mm  [stored 0.127953 ft]; Profile1_Height=380 mm; Profile1_Length=19 mm  [stored 0.062336 ft]; Profile1_Length_2=13 mm; Profile_Dia=10 mm  [stored 0.0328084 ft]; Profile_Dia_2=10 mm  [stored 0.0328084 ft]; Profile_Dia_3=20 mm  [stored 0.0656168 ft]; Top_Profile=340 mm; Top_Profile_Ref=345 mm; Top_Profile_Ref_2=73 mm; Top_Profile_Ref_3=490 mm; W=590 mm; W_Ref=583 mm
- 879-0300-10-144009D9C99_DN300_PN16: Body_Collar_Dia=89 mm; Body_Collar_Dia_2=57 mm; Body_Flange_Dia=236 mm; Body_Flange_Dia_2=258 mm; Body_Height_1=213 mm; Body_Height_2=106 mm; Body_Height_3=95 mm; Body_Height_4=121 mm; Body_Top_Dia=34 mm; Body_Top_Dia_2=28 mm  [stored 0.0918635 ft]; Body_With_Dia=213 mm; Body_With_Dia_2=213 mm; Bolt_support=567 mm; Bolt_support_2=283 mm; Bolt_support_Dia=25 mm  [stored 0.082021 ft]; Bolt_support_lenght=170 mm; Bolt_support_lenght_2=180 mm; Bottom_profile=75 mm; D1=185 mm; D3=230 mm; DN=300 mm; Fillet_Length=10 mm  [stored 0.0328084 ft]; Flange_thickness=25 mm  [stored 0.082021 ft]; H3=761 mm; H3_ref=756 mm; ID=150 mm; ID_2=116 mm; L=850 mm; L_ref=354 mm; PG_Dia=100 mm; PG_Ref=142 mm; PG_depth=14 mm  [stored 0.0459318 ft]; PG_ref=160 mm; Pilot_Dia_1=55 mm; Pilot_Dia_2=109 mm; Pilot_Dia_3=36 mm; Pilot_Dia_4=18 mm; Pilot_Dia_5=12 mm  [stored 0.0393701 ft]; Pilot_top_1=487 mm; Pilot_top_ref=39 mm  [stored 0.127953 ft]; Profile1_Height=380 mm; Profile1_Length=19 mm  [stored 0.062336 ft]; Profile1_Length_2=13 mm; Profile_Dia=10 mm  [stored 0.0328084 ft]; Profile_Dia_2=10 mm  [stored 0.0328084 ft]; Profile_Dia_3=20 mm  [stored 0.0656168 ft]; Top_Profile=340 mm; Top_Profile_Ref=345 mm; Top_Profile_Ref_2=73 mm; Top_Profile_Ref_3=490 mm; W=590 mm; W_Ref=583 mm
- 879-0350-10-044009A9C99_DN350_PN10: Body_Collar_Dia=102 mm; Body_Collar_Dia_2=65 mm; Body_Flange_Dia=272 mm; Body_Flange_Dia_2=297 mm; Body_Height_1=245 mm; Body_Height_2=123 mm; Body_Height_3=98 mm; Body_Height_4=138 mm; Body_Top_Dia=39 mm  [stored 0.127953 ft]; Body_Top_Dia_2=33 mm; Body_With_Dia=245 mm; Body_With_Dia_2=245 mm; Bolt_support=653 mm; Bolt_support_2=327 mm; Bolt_support_Dia=38 mm; Bolt_support_lenght=195 mm; Bolt_support_lenght_2=205 mm; Bottom_profile=88 mm; D1=215 mm; D3=253 mm; DN=350 mm; Fillet_Length=15 mm  [stored 0.0492126 ft]; Flange_thickness=27 mm; H3=883 mm; H3_ref=876 mm; ID=175 mm; ID_2=135 mm; L=980 mm; L_ref=408 mm; PG_Dia=117 mm; PG_Ref=163 mm; PG_depth=21 mm  [stored 0.0688976 ft]; PG_ref=185 mm; Pilot_Dia_1=61 mm; Pilot_Dia_2=121 mm; Pilot_Dia_3=40 mm  [stored 0.131234 ft]; Pilot_Dia_4=20 mm  [stored 0.0656168 ft]; Pilot_Dia_5=13 mm; Pilot_top_1=562 mm; Pilot_top_ref=61 mm; Profile1_Height=430 mm; Profile1_Length=21 mm  [stored 0.0688976 ft]; Profile1_Length_2=14 mm  [stored 0.0459318 ft]; Profile_Dia=15 mm  [stored 0.0492126 ft]; Profile_Dia_2=15 mm  [stored 0.0492126 ft]; Profile_Dia_3=30 mm  [stored 0.0984252 ft]; Top_Profile=392 mm; Top_Profile_Ref=397 mm; Top_Profile_Ref_2=97 mm; Top_Profile_Ref_3=575 mm; W=650 mm; W_Ref=640 mm
- 879-0350-10-044009D9C99_DN350_PN10: Body_Collar_Dia=102 mm; Body_Collar_Dia_2=65 mm; Body_Flange_Dia=272 mm; Body_Flange_Dia_2=297 mm; Body_Height_1=245 mm; Body_Height_2=123 mm; Body_Height_3=98 mm; Body_Height_4=138 mm; Body_Top_Dia=39 mm  [stored 0.127953 ft]; Body_Top_Dia_2=33 mm; Body_With_Dia=245 mm; Body_With_Dia_2=245 mm; Bolt_support=653 mm; Bolt_support_2=327 mm; Bolt_support_Dia=38 mm; Bolt_support_lenght=195 mm; Bolt_support_lenght_2=205 mm; Bottom_profile=88 mm; D1=215 mm; D3=253 mm; DN=350 mm; Fillet_Length=15 mm  [stored 0.0492126 ft]; Flange_thickness=27 mm; H3=883 mm; H3_ref=876 mm; ID=175 mm; ID_2=135 mm; L=980 mm; L_ref=408 mm; PG_Dia=117 mm; PG_Ref=163 mm; PG_depth=21 mm  [stored 0.0688976 ft]; PG_ref=185 mm; Pilot_Dia_1=61 mm; Pilot_Dia_2=121 mm; Pilot_Dia_3=40 mm  [stored 0.131234 ft]; Pilot_Dia_4=20 mm  [stored 0.0656168 ft]; Pilot_Dia_5=13 mm; Pilot_top_1=562 mm; Pilot_top_ref=61 mm; Profile1_Height=430 mm; Profile1_Length=21 mm  [stored 0.0688976 ft]; Profile1_Length_2=14 mm  [stored 0.0459318 ft]; Profile_Dia=15 mm  [stored 0.0492126 ft]; Profile_Dia_2=15 mm  [stored 0.0492126 ft]; Profile_Dia_3=30 mm  [stored 0.0984252 ft]; Top_Profile=392 mm; Top_Profile_Ref=397 mm; Top_Profile_Ref_2=97 mm; Top_Profile_Ref_3=575 mm; W=650 mm; W_Ref=640 mm
- 879-0350-10-144009A9C99_DN350_PN16: Body_Collar_Dia=102 mm; Body_Collar_Dia_2=65 mm; Body_Flange_Dia=272 mm; Body_Flange_Dia_2=297 mm; Body_Height_1=245 mm; Body_Height_2=123 mm; Body_Height_3=89 mm; Body_Height_4=138 mm; Body_Top_Dia=39 mm  [stored 0.127953 ft]; Body_Top_Dia_2=33 mm; Body_With_Dia=245 mm; Body_With_Dia_2=245 mm; Bolt_support=653 mm; Bolt_support_2=327 mm; Bolt_support_Dia=38 mm; Bolt_support_lenght=195 mm; Bolt_support_lenght_2=205 mm; Bottom_profile=88 mm; D1=215 mm; D3=260 mm; DN=350 mm; Fillet_Length=15 mm  [stored 0.0492126 ft]; Flange_thickness=27 mm; H3=883 mm; H3_ref=876 mm; ID=175 mm; ID_2=135 mm; L=980 mm; L_ref=408 mm; PG_Dia=117 mm; PG_Ref=163 mm; PG_depth=21 mm  [stored 0.0688976 ft]; PG_ref=185 mm; Pilot_Dia_1=63 mm; Pilot_Dia_2=126 mm; Pilot_Dia_3=42 mm  [stored 0.137795 ft]; Pilot_Dia_4=21 mm  [stored 0.0688976 ft]; Pilot_Dia_5=14 mm  [stored 0.0459318 ft]; Pilot_top_1=554 mm; Pilot_top_ref=62 mm; Profile1_Height=430 mm; Profile1_Length=22 mm  [stored 0.0721785 ft]; Profile1_Length_2=14 mm  [stored 0.0459318 ft]; Profile_Dia=15 mm  [stored 0.0492126 ft]; Profile_Dia_2=15 mm  [stored 0.0492126 ft]; Profile_Dia_3=30 mm  [stored 0.0984252 ft]; Top_Profile=392 mm; Top_Profile_Ref=397 mm; Top_Profile_Ref_2=93 mm; Top_Profile_Ref_3=569 mm; W=650 mm; W_Ref=640 mm
- 879-0350-10-144009D9C99_DN350_PN16: Body_Collar_Dia=102 mm; Body_Collar_Dia_2=65 mm; Body_Flange_Dia=272 mm; Body_Flange_Dia_2=297 mm; Body_Height_1=245 mm; Body_Height_2=123 mm; Body_Height_3=89 mm; Body_Height_4=138 mm; Body_Top_Dia=39 mm  [stored 0.127953 ft]; Body_Top_Dia_2=33 mm; Body_With_Dia=245 mm; Body_With_Dia_2=245 mm; Bolt_support=653 mm; Bolt_support_2=327 mm; Bolt_support_Dia=38 mm; Bolt_support_lenght=195 mm; Bolt_support_lenght_2=205 mm; Bottom_profile=88 mm; D1=215 mm; D3=260 mm; DN=350 mm; Fillet_Length=15 mm  [stored 0.0492126 ft]; Flange_thickness=27 mm; H3=883 mm; H3_ref=876 mm; ID=175 mm; ID_2=135 mm; L=980 mm; L_ref=408 mm; PG_Dia=117 mm; PG_Ref=163 mm; PG_depth=21 mm  [stored 0.0688976 ft]; PG_ref=185 mm; Pilot_Dia_1=63 mm; Pilot_Dia_2=126 mm; Pilot_Dia_3=42 mm  [stored 0.137795 ft]; Pilot_Dia_4=21 mm  [stored 0.0688976 ft]; Pilot_Dia_5=14 mm  [stored 0.0459318 ft]; Pilot_top_1=554 mm; Pilot_top_ref=62 mm; Profile1_Height=430 mm; Profile1_Length=22 mm  [stored 0.0721785 ft]; Profile1_Length_2=14 mm  [stored 0.0459318 ft]; Profile_Dia=15 mm  [stored 0.0492126 ft]; Profile_Dia_2=15 mm  [stored 0.0492126 ft]; Profile_Dia_3=30 mm  [stored 0.0984252 ft]; Top_Profile=392 mm; Top_Profile_Ref=397 mm; Top_Profile_Ref_2=93 mm; Top_Profile_Ref_3=569 mm; W=650 mm; W_Ref=640 mm
- 879-0400-10-044009A9C99_DN400_PN10: Body_Collar_Dia=115 mm; Body_Collar_Dia_2=73 mm; Body_Flange_Dia=306 mm; Body_Flange_Dia_2=333 mm; Body_Height_1=275 mm; Body_Height_2=138 mm; Body_Height_3=110 mm; Body_Height_4=153 mm; Body_Top_Dia=44 mm; Body_Top_Dia_2=37 mm; Body_With_Dia=275 mm; Body_With_Dia_2=275 mm; Bolt_support=733 mm; Bolt_support_2=367 mm; Bolt_support_Dia=50 mm; Bolt_support_lenght=220 mm; Bolt_support_lenght_2=230 mm; Bottom_profile=100 mm; D1=240 mm; D3=283 mm; DN=400 mm; Fillet_Length=20 mm  [stored 0.0656168 ft]; Flange_thickness=28 mm  [stored 0.0918635 ft]; H3=945 mm; H3_ref=935 mm; ID=200 mm; ID_2=154 mm; L=1100 mm; L_ref=458 mm; PG_Dia=133 mm; PG_Ref=183 mm; PG_depth=28 mm  [stored 0.0918635 ft]; PG_ref=210 mm; Pilot_Dia_1=69 mm; Pilot_Dia_2=138 mm; Pilot_Dia_3=46 mm; Pilot_Dia_4=23 mm  [stored 0.0754593 ft]; Pilot_Dia_5=15 mm  [stored 0.0492126 ft]; Pilot_top_1=605 mm; Pilot_top_ref=48 mm; Profile1_Height=480 mm; Profile1_Length=24 mm  [stored 0.0787402 ft]; Profile1_Length_2=16 mm  [stored 0.0524934 ft]; Profile_Dia=20 mm  [stored 0.0656168 ft]; Profile_Dia_2=20 mm  [stored 0.0656168 ft]; Profile_Dia_3=40 mm  [stored 0.131234 ft]; Top_Profile=440 mm; Top_Profile_Ref=445 mm; Top_Profile_Ref_2=86 mm; Top_Profile_Ref_3=609 mm; W=710 mm; W_Ref=696 mm
- 879-0400-10-044009D9C99_DN400_PN10: Body_Collar_Dia=115 mm; Body_Collar_Dia_2=73 mm; Body_Flange_Dia=306 mm; Body_Flange_Dia_2=333 mm; Body_Height_1=275 mm; Body_Height_2=138 mm; Body_Height_3=122 mm; Body_Height_4=153 mm; Body_Top_Dia=44 mm; Body_Top_Dia_2=37 mm; Body_With_Dia=275 mm; Body_With_Dia_2=275 mm; Bolt_support=733 mm; Bolt_support_2=367 mm; Bolt_support_Dia=50 mm; Bolt_support_lenght=220 mm; Bolt_support_lenght_2=230 mm; Bottom_profile=100 mm; D1=240 mm; D3=283 mm; DN=400 mm; Fillet_Length=20 mm  [stored 0.0656168 ft]; Flange_thickness=28 mm  [stored 0.0918635 ft]; H3=945 mm; H3_ref=935 mm; ID=200 mm; ID_2=154 mm; L=1100 mm; L_ref=458 mm; PG_Dia=133 mm; PG_Ref=183 mm; PG_depth=28 mm  [stored 0.0918635 ft]; PG_ref=210 mm; Pilot_Dia_1=69 mm; Pilot_Dia_2=138 mm; Pilot_Dia_3=46 mm; Pilot_Dia_4=23 mm  [stored 0.0754593 ft]; Pilot_Dia_5=15 mm  [stored 0.0492126 ft]; Pilot_top_1=611 mm; Pilot_top_ref=42 mm  [stored 0.137795 ft]; Profile1_Height=480 mm; Profile1_Length=24 mm  [stored 0.0787402 ft]; Profile1_Length_2=16 mm  [stored 0.0524934 ft]; Profile_Dia=20 mm  [stored 0.0656168 ft]; Profile_Dia_2=20 mm  [stored 0.0656168 ft]; Profile_Dia_3=40 mm  [stored 0.131234 ft]; Top_Profile=440 mm; Top_Profile_Ref=445 mm; Top_Profile_Ref_2=86 mm; Top_Profile_Ref_3=609 mm; W=710 mm; W_Ref=696 mm
- 879-0400-10-144009A9C99_DN400_PN16: Body_Collar_Dia=115 mm; Body_Collar_Dia_2=73 mm; Body_Flange_Dia=306 mm; Body_Flange_Dia_2=333 mm; Body_Height_1=275 mm; Body_Height_2=138 mm; Body_Height_3=100 mm; Body_Height_4=153 mm; Body_Top_Dia=44 mm; Body_Top_Dia_2=37 mm; Body_With_Dia=275 mm; Body_With_Dia_2=275 mm; Bolt_support=733 mm; Bolt_support_2=367 mm; Bolt_support_Dia=50 mm; Bolt_support_lenght=220 mm; Bolt_support_lenght_2=230 mm; Bottom_profile=100 mm; D1=240 mm; D3=290 mm; DN=400 mm; Fillet_Length=20 mm  [stored 0.0656168 ft]; Flange_thickness=28 mm  [stored 0.0918635 ft]; H3=945 mm; H3_ref=935 mm; ID=200 mm; ID_2=154 mm; L=1100 mm; L_ref=458 mm; PG_Dia=133 mm; PG_Ref=183 mm; PG_depth=28 mm  [stored 0.0918635 ft]; PG_ref=210 mm; Pilot_Dia_1=71 mm; Pilot_Dia_2=142 mm; Pilot_Dia_3=47 mm; Pilot_Dia_4=24 mm  [stored 0.0787402 ft]; Pilot_Dia_5=16 mm  [stored 0.0524934 ft]; Pilot_top_1=596 mm; Pilot_top_ref=49 mm; Profile1_Height=480 mm; Profile1_Length=24 mm  [stored 0.0787402 ft]; Profile1_Length_2=16 mm  [stored 0.0524934 ft]; Profile_Dia=20 mm  [stored 0.0656168 ft]; Profile_Dia_2=20 mm  [stored 0.0656168 ft]; Profile_Dia_3=40 mm  [stored 0.131234 ft]; Top_Profile=440 mm; Top_Profile_Ref=445 mm; Top_Profile_Ref_2=83 mm; Top_Profile_Ref_3=604 mm; W=710 mm; W_Ref=696 mm
- 879-0400-10-144009D9C99_DN400_PN16: Body_Collar_Dia=115 mm; Body_Collar_Dia_2=73 mm; Body_Flange_Dia=306 mm; Body_Flange_Dia_2=333 mm; Body_Height_1=275 mm; Body_Height_2=138 mm; Body_Height_3=110 mm; Body_Height_4=153 mm; Body_Top_Dia=44 mm; Body_Top_Dia_2=37 mm; Body_With_Dia=275 mm; Body_With_Dia_2=275 mm; Bolt_support=733 mm; Bolt_support_2=367 mm; Bolt_support_Dia=50 mm; Bolt_support_lenght=220 mm; Bolt_support_lenght_2=230 mm; Bottom_profile=100 mm; D1=240 mm; D3=290 mm; DN=400 mm; Fillet_Length=20 mm  [stored 0.0656168 ft]; Flange_thickness=28 mm  [stored 0.0918635 ft]; H3=945 mm; H3_ref=935 mm; ID=200 mm; ID_2=154 mm; L=1100 mm; L_ref=458 mm; PG_Dia=133 mm; PG_Ref=183 mm; PG_depth=28 mm  [stored 0.0918635 ft]; PG_ref=210 mm; Pilot_Dia_1=71 mm; Pilot_Dia_2=142 mm; Pilot_Dia_3=47 mm; Pilot_Dia_4=24 mm  [stored 0.0787402 ft]; Pilot_Dia_5=16 mm  [stored 0.0524934 ft]; Pilot_top_1=601 mm; Pilot_top_ref=44 mm; Profile1_Height=400 mm; Profile1_Length=24 mm  [stored 0.0787402 ft]; Profile1_Length_2=16 mm  [stored 0.0524934 ft]; Profile_Dia=20 mm  [stored 0.0656168 ft]; Profile_Dia_2=20 mm  [stored 0.0656168 ft]; Profile_Dia_3=40 mm  [stored 0.131234 ft]; Top_Profile=440 mm; Top_Profile_Ref=445 mm; Top_Profile_Ref_2=123 mm; Top_Profile_Ref_3=584 mm; W=710 mm; W_Ref=696 mm
- 879-0450-10-044009A9C99_DN450_PN10: Body_Collar_Dia=125 mm; Body_Collar_Dia_2=80 mm; Body_Flange_Dia=333 mm; Body_Flange_Dia_2=364 mm; Body_Height_1=300 mm; Body_Height_2=150 mm; Body_Height_3=120 mm; Body_Height_4=165 mm; Body_Top_Dia=48 mm; Body_Top_Dia_2=40 mm  [stored 0.131234 ft]; Body_With_Dia=300 mm; Body_With_Dia_2=300 mm; Bolt_support=800 mm; Bolt_support_2=400 mm; Bolt_support_Dia=50 mm; Bolt_support_lenght=245 mm; Bolt_support_lenght_2=255 mm; Bottom_profile=113 mm; D1=265 mm; D3=308 mm; DN=450 mm; Fillet_Length=20 mm  [stored 0.0656168 ft]; Flange_thickness=30 mm  [stored 0.0984252 ft]; H3=1123 mm; H3_ref=1113 mm; ID=225 mm; ID_2=173 mm; L=1200 mm; L_ref=500 mm; PG_Dia=150 mm; PG_Ref=200 mm; PG_depth=28 mm  [stored 0.0918635 ft]; PG_ref=235 mm; Pilot_Dia_1=76 mm; Pilot_Dia_2=151 mm; Pilot_Dia_3=50 mm; Pilot_Dia_4=25 mm  [stored 0.082021 ft]; Pilot_Dia_5=17 mm; Pilot_top_1=705 mm; Pilot_top_ref=100 mm; Profile1_Height=509 mm; Profile1_Length=26 mm; Profile1_Length_2=17 mm; Profile_Dia=20 mm  [stored 0.0656168 ft]; Profile_Dia_2=20 mm  [stored 0.0656168 ft]; Profile_Dia_3=40 mm  [stored 0.131234 ft]; Top_Profile=480 mm; Top_Profile_Ref=485 mm; Top_Profile_Ref_2=148 mm; Top_Profile_Ref_3=731 mm; W=770 mm; W_Ref=756 mm
- 879-0450-10-044009D9C99_DN450_PN10: Body_Collar_Dia=125 mm; Body_Collar_Dia_2=80 mm; Body_Flange_Dia=333 mm; Body_Flange_Dia_2=364 mm; Body_Height_1=300 mm; Body_Height_2=150 mm; Body_Height_3=120 mm; Body_Height_4=165 mm; Body_Top_Dia=48 mm; Body_Top_Dia_2=40 mm  [stored 0.131234 ft]; Body_With_Dia=300 mm; Body_With_Dia_2=300 mm; Bolt_support=800 mm; Bolt_support_2=400 mm; Bolt_support_Dia=50 mm; Bolt_support_lenght=245 mm; Bolt_support_lenght_2=255 mm; Bottom_profile=113 mm; D1=265 mm; D3=308 mm; DN=450 mm; Fillet_Length=20 mm  [stored 0.0656168 ft]; Flange_thickness=30 mm  [stored 0.0984252 ft]; H3=1123 mm; H3_ref=1113 mm; ID=225 mm; ID_2=173 mm; L=1200 mm; L_ref=500 mm; PG_Dia=150 mm; PG_Ref=200 mm; PG_depth=28 mm  [stored 0.0918635 ft]; PG_ref=235 mm; Pilot_Dia_1=76 mm; Pilot_Dia_2=151 mm; Pilot_Dia_3=50 mm; Pilot_Dia_4=25 mm  [stored 0.082021 ft]; Pilot_Dia_5=17 mm; Pilot_top_1=705 mm; Pilot_top_ref=100 mm; Profile1_Height=531 mm; Profile1_Length=26 mm; Profile1_Length_2=17 mm; Profile_Dia=20 mm  [stored 0.0656168 ft]; Profile_Dia_2=20 mm  [stored 0.0656168 ft]; Profile_Dia_3=40 mm  [stored 0.131234 ft]; Top_Profile=480 mm; Top_Profile_Ref=485 mm; Top_Profile_Ref_2=138 mm; Top_Profile_Ref_3=737 mm; W=770 mm; W_Ref=756 mm
- 879-0450-10-144009A9C99_DN450_PN16: Body_Collar_Dia=125 mm; Body_Collar_Dia_2=80 mm; Body_Flange_Dia=333 mm; Body_Flange_Dia_2=364 mm; Body_Height_1=300 mm; Body_Height_2=150 mm; Body_Height_3=120 mm; Body_Height_4=165 mm; Body_Top_Dia=48 mm; Body_Top_Dia_2=40 mm  [stored 0.131234 ft]; Body_With_Dia=300 mm; Body_With_Dia_2=300 mm; Bolt_support=800 mm; Bolt_support_2=400 mm; Bolt_support_Dia=50 mm; Bolt_support_lenght=245 mm; Bolt_support_lenght_2=255 mm; Bottom_profile=113 mm; D1=274 mm; D3=320 mm; DN=450 mm; Fillet_Length=20 mm  [stored 0.0656168 ft]; Flange_thickness=30 mm  [stored 0.0984252 ft]; H3=1123 mm; H3_ref=1113 mm; ID=225 mm; ID_2=173 mm; L=1200 mm; L_ref=500 mm; PG_Dia=150 mm; PG_Ref=200 mm; PG_depth=28 mm  [stored 0.0918635 ft]; PG_ref=235 mm; Pilot_Dia_1=79 mm; Pilot_Dia_2=158 mm; Pilot_Dia_3=53 mm; Pilot_Dia_4=26 mm; Pilot_Dia_5=18 mm; Pilot_top_1=699 mm; Pilot_top_ref=94 mm; Profile1_Height=530 mm; Profile1_Length=27 mm; Profile1_Length_2=18 mm; Profile_Dia=20 mm  [stored 0.0656168 ft]; Profile_Dia_2=20 mm  [stored 0.0656168 ft]; Profile_Dia_3=40 mm  [stored 0.131234 ft]; Top_Profile=480 mm; Top_Profile_Ref=485 mm; Top_Profile_Ref_2=132 mm; Top_Profile_Ref_3=727 mm; W=770 mm; W_Ref=756 mm
- 879-0450-10-144009D9C99_DN450_PN16: Body_Collar_Dia=125 mm; Body_Collar_Dia_2=80 mm; Body_Flange_Dia=333 mm; Body_Flange_Dia_2=364 mm; Body_Height_1=300 mm; Body_Height_2=150 mm; Body_Height_3=120 mm; Body_Height_4=165 mm; Body_Top_Dia=48 mm; Body_Top_Dia_2=40 mm  [stored 0.131234 ft]; Body_With_Dia=300 mm; Body_With_Dia_2=300 mm; Bolt_support=800 mm; Bolt_support_2=400 mm; Bolt_support_Dia=50 mm; Bolt_support_lenght=245 mm; Bolt_support_lenght_2=255 mm; Bottom_profile=113 mm; D1=274 mm; D3=320 mm; DN=450 mm; Fillet_Length=20 mm  [stored 0.0656168 ft]; Flange_thickness=30 mm  [stored 0.0984252 ft]; H3=1123 mm; H3_ref=1113 mm; ID=225 mm; ID_2=173 mm; L=1200 mm; L_ref=500 mm; PG_Dia=150 mm; PG_Ref=200 mm; PG_depth=28 mm  [stored 0.0918635 ft]; PG_ref=235 mm; Pilot_Dia_1=79 mm; Pilot_Dia_2=158 mm; Pilot_Dia_3=53 mm; Pilot_Dia_4=26 mm; Pilot_Dia_5=18 mm; Pilot_top_1=699 mm; Pilot_top_ref=94 mm; Profile1_Height=531 mm; Profile1_Length=27 mm; Profile1_Length_2=18 mm; Profile_Dia=20 mm  [stored 0.0656168 ft]; Profile_Dia_2=20 mm  [stored 0.0656168 ft]; Profile_Dia_3=40 mm  [stored 0.131234 ft]; Top_Profile=480 mm; Top_Profile_Ref=485 mm; Top_Profile_Ref_2=131 mm; Top_Profile_Ref_3=727 mm; W=770 mm; W_Ref=756 mm
- 879-0500-10-044009A9C99_DN500_PN10: Body_Collar_Dia=130 mm; Body_Collar_Dia_2=83 mm; Body_Flange_Dia=347 mm; Body_Flange_Dia_2=379 mm; Body_Height_1=313 mm; Body_Height_2=156 mm; Body_Height_3=125 mm; Body_Height_4=171 mm; Body_Top_Dia=50 mm; Body_Top_Dia_2=42 mm  [stored 0.137795 ft]; Body_With_Dia=313 mm; Body_With_Dia_2=313 mm; Bolt_support=833 mm; Bolt_support_2=417 mm; Bolt_support_Dia=63 mm; Bolt_support_lenght=270 mm; Bolt_support_lenght_2=280 mm; Bottom_profile=125 mm; D1=291 mm; D3=335 mm; DN=500 mm; Fillet_Length=25 mm  [stored 0.082021 ft]; Flange_thickness=32 mm  [stored 0.104987 ft]; H3=1197 mm; H3_ref=1185 mm; ID=250 mm; ID_2=192 mm; L=1250 mm; L_ref=521 mm; PG_Dia=167 mm; PG_Ref=208 mm; PG_depth=35 mm  [stored 0.114829 ft]; PG_ref=260 mm; Pilot_Dia_1=83 mm; Pilot_Dia_2=166 mm; Pilot_Dia_3=55 mm; Pilot_Dia_4=28 mm  [stored 0.0918635 ft]; Pilot_Dia_5=18 mm; Pilot_top_1=739 mm; Pilot_top_ref=110 mm; Profile1_Height=541 mm; Profile1_Length=28 mm  [stored 0.0918635 ft]; Profile1_Length_2=19 mm  [stored 0.062336 ft]; Profile_Dia=25 mm  [stored 0.082021 ft]; Profile_Dia_2=25 mm  [stored 0.082021 ft]; Profile_Dia_3=50 mm; Top_Profile=500 mm; Top_Profile_Ref=505 mm; Top_Profile_Ref_2=154 mm; Top_Profile_Ref_3=772 mm; W=845 mm; W_Ref=828 mm
- 879-0500-10-044009D9C99_DN500_PN10: Body_Collar_Dia=130 mm; Body_Collar_Dia_2=83 mm; Body_Flange_Dia=347 mm; Body_Flange_Dia_2=379 mm; Body_Height_1=313 mm; Body_Height_2=156 mm; Body_Height_3=125 mm; Body_Height_4=171 mm; Body_Top_Dia=50 mm; Body_Top_Dia_2=42 mm  [stored 0.137795 ft]; Body_With_Dia=313 mm; Body_With_Dia_2=313 mm; Bolt_support=833 mm; Bolt_support_2=417 mm; Bolt_support_Dia=63 mm; Bolt_support_lenght=270 mm; Bolt_support_lenght_2=280 mm; Bottom_profile=125 mm; D1=291 mm; D3=335 mm; DN=500 mm; Fillet_Length=25 mm  [stored 0.082021 ft]; Flange_thickness=32 mm  [stored 0.104987 ft]; H3=1197 mm; H3_ref=1185 mm; ID=250 mm; ID_2=192 mm; L=1250 mm; L_ref=521 mm; PG_Dia=167 mm; PG_Ref=208 mm; PG_depth=35 mm  [stored 0.114829 ft]; PG_ref=260 mm; Pilot_Dia_1=83 mm; Pilot_Dia_2=166 mm; Pilot_Dia_3=55 mm; Pilot_Dia_4=28 mm  [stored 0.0918635 ft]; Pilot_Dia_5=18 mm; Pilot_top_1=739 mm; Pilot_top_ref=110 mm; Profile1_Height=541 mm; Profile1_Length=28 mm  [stored 0.0918635 ft]; Profile1_Length_2=19 mm  [stored 0.062336 ft]; Profile_Dia=25 mm  [stored 0.082021 ft]; Profile_Dia_2=25 mm  [stored 0.082021 ft]; Profile_Dia_3=50 mm; Top_Profile=500 mm; Top_Profile_Ref=505 mm; Top_Profile_Ref_2=154 mm; Top_Profile_Ref_3=772 mm; W=845 mm; W_Ref=828 mm
- 879-0500-10-144009A9C99_DN500_PN16: Body_Collar_Dia=130 mm; Body_Collar_Dia_2=83 mm; Body_Flange_Dia=347 mm; Body_Flange_Dia_2=379 mm; Body_Height_1=313 mm; Body_Height_2=156 mm; Body_Height_3=125 mm; Body_Height_4=171 mm; Body_Top_Dia=50 mm; Body_Top_Dia_2=42 mm  [stored 0.137795 ft]; Body_With_Dia=313 mm; Body_With_Dia_2=313 mm; Bolt_support=833 mm; Bolt_support_2=417 mm; Bolt_support_Dia=63 mm; Bolt_support_lenght=270 mm; Bolt_support_lenght_2=280 mm; Bottom_profile=125 mm; D1=305 mm; D3=358 mm; DN=500 mm; Fillet_Length=25 mm  [stored 0.082021 ft]; Flange_thickness=32 mm  [stored 0.104987 ft]; H3=1197 mm; H3_ref=1185 mm; ID=250 mm; ID_2=192 mm; L=1250 mm; L_ref=521 mm; PG_Dia=167 mm; PG_Ref=208 mm; PG_depth=35 mm  [stored 0.114829 ft]; PG_ref=260 mm; Pilot_Dia_1=80 mm; Pilot_Dia_2=160 mm; Pilot_Dia_3=53 mm; Pilot_Dia_4=27 mm; Pilot_Dia_5=18 mm; Pilot_top_1=728 mm; Pilot_top_ref=99 mm; Profile1_Height=541 mm; Profile1_Length=30 mm  [stored 0.0984252 ft]; Profile1_Length_2=20 mm  [stored 0.0656168 ft]; Profile_Dia=25 mm  [stored 0.082021 ft]; Profile_Dia_2=25 mm  [stored 0.082021 ft]; Profile_Dia_3=50 mm; Top_Profile=500 mm; Top_Profile_Ref=505 mm; Top_Profile_Ref_2=143 mm; Top_Profile_Ref_3=756 mm; W=845 mm; W_Ref=828 mm
- 879-0500-10-144009D9C99_DN500_PN16: Body_Collar_Dia=130 mm; Body_Collar_Dia_2=83 mm; Body_Flange_Dia=347 mm; Body_Flange_Dia_2=379 mm; Body_Height_1=313 mm; Body_Height_2=156 mm; Body_Height_3=125 mm; Body_Height_4=171 mm; Body_Top_Dia=50 mm; Body_Top_Dia_2=42 mm  [stored 0.137795 ft]; Body_With_Dia=313 mm; Body_With_Dia_2=313 mm; Bolt_support=833 mm; Bolt_support_2=417 mm; Bolt_support_Dia=63 mm; Bolt_support_lenght=270 mm; Bolt_support_lenght_2=280 mm; Bottom_profile=125 mm; D1=305 mm; D3=358 mm; DN=500 mm; Fillet_Length=25 mm  [stored 0.082021 ft]; Flange_thickness=32 mm  [stored 0.104987 ft]; H3=1197 mm; H3_ref=1185 mm; ID=250 mm; ID_2=192 mm; L=1250 mm; L_ref=521 mm; PG_Dia=167 mm; PG_Ref=208 mm; PG_depth=35 mm  [stored 0.114829 ft]; PG_ref=260 mm; Pilot_Dia_1=80 mm; Pilot_Dia_2=160 mm; Pilot_Dia_3=53 mm; Pilot_Dia_4=27 mm; Pilot_Dia_5=18 mm; Pilot_top_1=728 mm; Pilot_top_ref=99 mm; Profile1_Height=563 mm; Profile1_Length=30 mm  [stored 0.0984252 ft]; Profile1_Length_2=20 mm  [stored 0.0656168 ft]; Profile_Dia=25 mm  [stored 0.082021 ft]; Profile_Dia_2=25 mm  [stored 0.082021 ft]; Profile_Dia_3=50 mm; Top_Profile=500 mm; Top_Profile_Ref=505 mm; Top_Profile_Ref_2=132 mm; Top_Profile_Ref_3=761 mm; W=845 mm; W_Ref=828 mm
- 879-0600-10-044009A9C99_DN600_PN10: Body_Collar_Dia=151 mm; Body_Collar_Dia_2=97 mm; Body_Flange_Dia=403 mm; Body_Flange_Dia_2=439 mm; Body_Height_1=363 mm; Body_Height_2=181 mm; Body_Height_3=145 mm; Body_Height_4=196 mm; Body_Top_Dia=58 mm; Body_Top_Dia_2=48 mm; Body_With_Dia=363 mm; Body_With_Dia_2=363 mm; Bolt_support=967 mm; Bolt_support_2=483 mm; Bolt_support_Dia=75 mm; Bolt_support_lenght=320 mm; Bolt_support_lenght_2=330 mm; Bottom_profile=150 mm; D1=341 mm; D3=390 mm; DN=600 mm; Fillet_Length=30 mm  [stored 0.0984252 ft]; Flange_thickness=36 mm; H3=1346 mm; H3_ref=1331 mm; ID=300 mm; ID_2=231 mm; L=1450 mm; L_ref=604 mm; PG_Dia=200 mm; PG_Ref=242 mm; PG_depth=42 mm  [stored 0.137795 ft]; PG_ref=310 mm; Pilot_Dia_1=98 mm; Pilot_Dia_2=196 mm; Pilot_Dia_3=65 mm; Pilot_Dia_4=33 mm; Pilot_Dia_5=22 mm  [stored 0.0721785 ft]; Pilot_top_1=832 mm; Pilot_top_ref=109 mm; Profile1_Height=616 mm; Profile1_Length=33 mm; Profile1_Length_2=22 mm  [stored 0.0721785 ft]; Profile_Dia=30 mm  [stored 0.0984252 ft]; Profile_Dia_2=30 mm  [stored 0.0984252 ft]; Profile_Dia_3=60 mm; Top_Profile=580 mm; Top_Profile_Ref=585 mm; Top_Profile_Ref_2=163 mm; Top_Profile_Ref_3=860 mm; W=970 mm; W_Ref=949 mm
- 879-0600-10-044009D9C99_DN600_PN10: Body_Collar_Dia=151 mm; Body_Collar_Dia_2=97 mm; Body_Flange_Dia=403 mm; Body_Flange_Dia_2=439 mm; Body_Height_1=363 mm; Body_Height_2=181 mm; Body_Height_3=145 mm; Body_Height_4=196 mm; Body_Top_Dia=58 mm; Body_Top_Dia_2=48 mm; Body_With_Dia=363 mm; Body_With_Dia_2=363 mm; Bolt_support=967 mm; Bolt_support_2=483 mm; Bolt_support_Dia=75 mm; Bolt_support_lenght=320 mm; Bolt_support_lenght_2=330 mm; Bottom_profile=150 mm; D1=341 mm; D3=390 mm; DN=600 mm; Fillet_Length=30 mm  [stored 0.0984252 ft]; Flange_thickness=36 mm; H3=1346 mm; H3_ref=1331 mm; ID=300 mm; ID_2=231 mm; L=1450 mm; L_ref=604 mm; PG_Dia=200 mm; PG_Ref=242 mm; PG_depth=42 mm  [stored 0.137795 ft]; PG_ref=310 mm; Pilot_Dia_1=98 mm; Pilot_Dia_2=196 mm; Pilot_Dia_3=65 mm; Pilot_Dia_4=33 mm; Pilot_Dia_5=22 mm  [stored 0.0721785 ft]; Pilot_top_1=832 mm; Pilot_top_ref=109 mm; Profile1_Height=660 mm; Profile1_Length=33 mm; Profile1_Length_2=22 mm  [stored 0.0721785 ft]; Profile_Dia=30 mm  [stored 0.0984252 ft]; Profile_Dia_2=30 mm  [stored 0.0984252 ft]; Profile_Dia_3=60 mm; Top_Profile=580 mm; Top_Profile_Ref=585 mm; Top_Profile_Ref_2=141 mm; Top_Profile_Ref_3=871 mm; W=970 mm; W_Ref=949 mm
- 879-0600-10-144009A9C99_DN600_PN16: Body_Collar_Dia=151 mm; Body_Collar_Dia_2=97 mm; Body_Flange_Dia=403 mm; Body_Flange_Dia_2=439 mm; Body_Height_1=363 mm; Body_Height_2=181 mm; Body_Height_3=145 mm; Body_Height_4=196 mm; Body_Top_Dia=58 mm; Body_Top_Dia_2=48 mm; Body_With_Dia=363 mm; Body_With_Dia_2=363 mm; Bolt_support=967 mm; Bolt_support_2=483 mm; Bolt_support_Dia=75 mm; Bolt_support_lenght=320 mm; Bolt_support_lenght_2=330 mm; Bottom_profile=150 mm; D1=360 mm; D3=420 mm; DN=600 mm; Fillet_Length=30 mm  [stored 0.0984252 ft]; Flange_thickness=36 mm; H3=1346 mm; H3_ref=1331 mm; ID=300 mm; ID_2=231 mm; L=1450 mm; L_ref=604 mm; PG_Dia=200 mm; PG_Ref=242 mm; PG_depth=42 mm  [stored 0.137795 ft]; PG_ref=310 mm; Pilot_Dia_1=80 mm; Pilot_Dia_2=160 mm; Pilot_Dia_3=53 mm; Pilot_Dia_4=27 mm; Pilot_Dia_5=18 mm; Pilot_top_1=817 mm; Pilot_top_ref=94 mm; Profile1_Height=616 mm; Profile1_Length=35 mm  [stored 0.114829 ft]; Profile1_Length_2=23 mm  [stored 0.0754593 ft]; Profile_Dia=30 mm  [stored 0.0984252 ft]; Profile_Dia_2=30 mm  [stored 0.0984252 ft]; Profile_Dia_3=60 mm; Top_Profile=580 mm; Top_Profile_Ref=585 mm; Top_Profile_Ref_2=148 mm; Top_Profile_Ref_3=837 mm; W=970 mm; W_Ref=949 mm
- 879-0600-10-144009D9C99_DN600_PN16: Body_Collar_Dia=151 mm; Body_Collar_Dia_2=97 mm; Body_Flange_Dia=403 mm; Body_Flange_Dia_2=439 mm; Body_Height_1=363 mm; Body_Height_2=181 mm; Body_Height_3=145 mm; Body_Height_4=196 mm; Body_Top_Dia=58 mm; Body_Top_Dia_2=48 mm; Body_With_Dia=363 mm; Body_With_Dia_2=363 mm; Bolt_support=967 mm; Bolt_support_2=483 mm; Bolt_support_Dia=75 mm; Bolt_support_lenght=320 mm; Bolt_support_lenght_2=330 mm; Bottom_profile=150 mm; D1=360 mm; D3=420 mm; DN=600 mm; Fillet_Length=30 mm  [stored 0.0984252 ft]; Flange_thickness=36 mm; H3=1346 mm; H3_ref=1331 mm; ID=300 mm; ID_2=231 mm; L=1450 mm; L_ref=604 mm; PG_Dia=200 mm; PG_Ref=242 mm; PG_depth=42 mm  [stored 0.137795 ft]; PG_ref=310 mm; Pilot_Dia_1=80 mm; Pilot_Dia_2=160 mm; Pilot_Dia_3=53 mm; Pilot_Dia_4=27 mm; Pilot_Dia_5=18 mm; Pilot_top_1=817 mm; Pilot_top_ref=94 mm; Profile1_Height=660 mm; Profile1_Length=35 mm  [stored 0.114829 ft]; Profile1_Length_2=23 mm  [stored 0.0754593 ft]; Profile_Dia=30 mm  [stored 0.0984252 ft]; Profile_Dia_2=30 mm  [stored 0.0984252 ft]; Profile_Dia_3=60 mm; Top_Profile=580 mm; Top_Profile_Ref=585 mm; Top_Profile_Ref_2=126 mm; Top_Profile_Ref_3=848 mm; W=970 mm; W_Ref=949 mm

note: [stored X ft] marks values corroborated as IEEE doubles in the binary element streams (Revit-internal decimal feet)

## geometry (parser evidence)
native form markers: Sweep x6
no freeform markers — native parametric forms only
